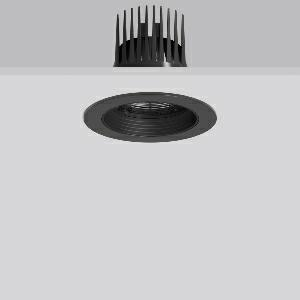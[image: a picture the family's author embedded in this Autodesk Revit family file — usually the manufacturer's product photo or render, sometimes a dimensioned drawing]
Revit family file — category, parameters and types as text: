
# Revit family: heledon_maxi_e_901774_003_57e2
name_source: partatom
category: Lighting Fixtures
units: mm (PartAtom-declared; Revit-internal decimal feet)

## family parameters
Cut with Voids When Loaded = No
Host = Face
Light Source = No
Part Type = Normal
Room Calculation Point = No
Round Connector Dimension = Use Diameter
Shared = No

## types (1)
- HELEDON maxi E (1 x LED Modul 932 fresh meat, 1800 lm, 3200)
    Apparent Load = 33 VA
    Approval mark = CE
    CIE Flux Codes = 97 100 100 100 100
    Color Rendering = 90
    Color Temperature = 3200
    Default Elevation = 1800 mm  [stored 5.90551 ft]
    Description = Series: HELEDON maxi
Round recessed downlight. Housing: die-cast aluminium, powder-coated. Black plastic ring and recessed LED to prevent glare from the side. Optical assembly with lens made of plastic (polycarbonate) for the best homogeneous light distribution - can be changed without tools. Special LED for illumination of meat included. Suitable for Recessed ceiling mounting. Installation without tools thanks to spring fastening system. Including separate LED converter with connecting cable 600 mm.High quality converter without flickering and stroboscopic effect. Through-wiring box (5 pole) available as accessory. The following accessories can be mounted without use of tools: interchangeable lenses, decorative glasses, honeycomb louvre, clear and frosted diffusers, white interchangeable plastic ring. 
Colour: deep black, matt (RAL 9005)
Diameter: 162 mm
Height: 3 mm
Cut-out diameter: 152 mm
Recess height: 200 mm
Luminaire: recess height: 135 mm
Lamp: LED
Socket: without socket
Colour temperature: fresh meat
System power: 33 W
Rated luminous flux: 1800 lm
Luminous efficiency: 55 lm/W
Control gear: Regulated power supply
Protection class: II
Type of protection: IP 20
    Height = 0 mm  [stored 0 ft]
    Lamp = 1 x LED Modul 932 fresh meat
    Lamp Light Flux = 1800 lm
    Lamp count = 1
    Length = 162 mm
    Lifetime = 50000 h
    Luminous efficacy = 55 lm/W
    Manufacturer = RZB
    ModVariant = No
    Model = 901774.003
    Mounting Place = Ceiling
    Mounting Type = Recessed
    Number of Poles = 1
    OnlyDefault = Yes
    Power Factor = 1
    Product Name = HELEDON maxi E
    Product group = Recessed downlights
    ProductGroupID = 402
    Protection Class = Protection class II
    Protection Degree = IP 20
    RLX_Detail_Level = 1
    RLX_Emergency_Light_Flux = 0 lm
    RLX_Emergency_Type = 0
    RLX_Emergency_Type_DB = No
    RlxData = <blob elided: 121789 chars, md5=d5e3d930>
    Socket = socket
    Standby Power = 0 W
    System Light Flux = 1800 lm
    System Power = 33 W
    Type Comments = Product without accessories
    Type Image = 901663.003.jpg
    URL = http://relux.com
    VarID = ---
    Voltage = 230 V
    Voltage Range = 220-240 V
    Weight = 0.00 kg
    Width = 0 mm  [stored 0 ft]

note: [stored X ft] marks values corroborated as IEEE doubles in the binary element streams (Revit-internal decimal feet)

## geometry (parser evidence)
native form markers: Blend x4, Sweep x13
no freeform markers — native parametric forms only
